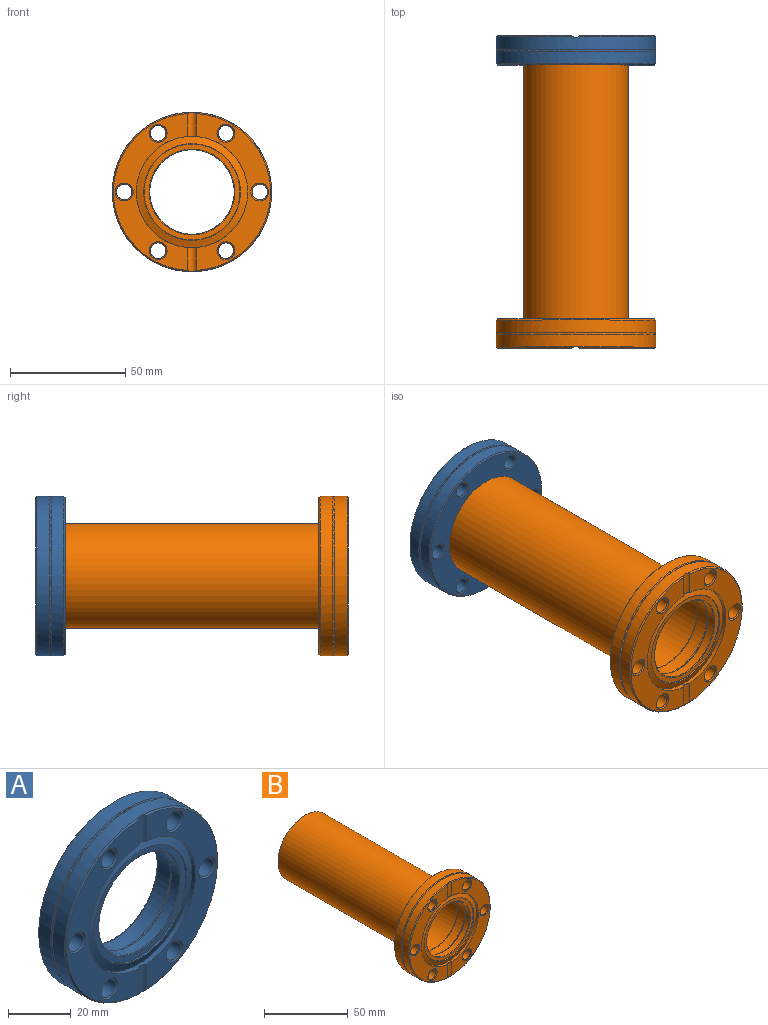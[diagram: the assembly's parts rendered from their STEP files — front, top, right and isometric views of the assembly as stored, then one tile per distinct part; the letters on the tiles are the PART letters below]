
ASSEMBLY  parts=2 mates=1
PART A: 41 faces, bbox 75.3x12.7x75.3 mm
  f0: cylinder r=34.54mm len=69.09mm, axis (0,-1,0), area 1172.5mm2, adj f1,f2,f5,f11,f36
  f1: cylinder r=2.38mm len=10.46mm, axis (0,0,1), area 41.3mm2, adj f0,f2,f3,f4,f5,f6
  f2: cone r=34.54mm half-angle=45deg, axis (0,1,0), area 75.3mm2, adj f0,f1,f3,f11
  f3: plane 67.98x32.27mm, normal (0,-1,0), area 728.6mm2, adj f1,f2,f4,f11,f12,f15,f18
  f4: cylinder r=24.13mm len=48.26mm, axis (0,1,0), area 275.3mm2, adj f1,f3,f6,f11,f38
  f5: cone r=34.54mm half-angle=45deg, axis (0,1,0), area 75.3mm2, adj f0,f1,f6,f11
  f6: plane 67.98x32.27mm, normal (0,-1,0), area 728.6mm2, adj f1,f4,f5,f11,f21,f24,f27
  f7: cylinder r=34.54mm len=69.09mm, axis (0,-1,0), area 1172.5mm2, adj f33,f36
  f8: plane 68.07x68.07mm, normal (0,1,0), area 2139.2mm2, adj f13,f16,f19,f22,f25,f28,f30,f33
  f9: cylinder r=19.18mm len=38.35mm, axis (0,1,0), area 696.9mm2, adj f30,f35
  f10: cylinder r=18.29mm len=36.58mm, axis (0,-1,0), area 423.2mm2, adj f31,f32
  f11: cylinder r=2.38mm len=10.46mm, axis (0,0,-1), area 41.3mm2, adj f0,f2,f3,f4,f5,f6
  f12: cone r=3.87mm half-angle=45deg, axis (0,-1,0), area 16.3mm2, adj f3,f14
  f13: cone r=3.37mm half-angle=45deg, axis (0,1,0), area 16.3mm2, adj f8,f14
  f14: cylinder r=3.37mm len=11.68mm, axis (0,-1,0), area 247.1mm2, adj f12,f13
  f15: cone r=3.87mm half-angle=45deg, axis (0,-1,0), area 16.3mm2, adj f3,f17
  f16: cone r=3.37mm half-angle=45deg, axis (0,1,0), area 16.3mm2, adj f8,f17
  f17: cylinder r=3.37mm len=11.68mm, axis (0,-1,0), area 247.1mm2, adj f15,f16
  f18: cone r=3.87mm half-angle=45deg, axis (0,-1,0), area 16.3mm2, adj f3,f20
  f19: cone r=3.37mm half-angle=45deg, axis (0,1,0), area 16.3mm2, adj f8,f20
  f20: cylinder r=3.37mm len=11.68mm, axis (0,-1,0), area 247.1mm2, adj f18,f19
  f21: cone r=3.87mm half-angle=45deg, axis (0,-1,0), area 16.3mm2, adj f6,f23
  f22: cone r=3.37mm half-angle=45deg, axis (0,1,0), area 16.3mm2, adj f8,f23
  f23: cylinder r=3.37mm len=11.68mm, axis (0,-1,0), area 247.1mm2, adj f21,f22
  f24: cone r=3.87mm half-angle=45deg, axis (0,-1,0), area 16.3mm2, adj f6,f26
  f25: cone r=3.37mm half-angle=45deg, axis (0,1,0), area 16.3mm2, adj f8,f26
  f26: cylinder r=3.37mm len=11.68mm, axis (0,-1,0), area 247.1mm2, adj f24,f25
  f27: cone r=3.87mm half-angle=45deg, axis (0,-1,0), area 16.3mm2, adj f6,f29
  f28: cone r=3.37mm half-angle=45deg, axis (0,1,0), area 16.3mm2, adj f8,f29
  f29: cylinder r=3.37mm len=11.68mm, axis (0,-1,0), area 247.1mm2, adj f27,f28
  f30: torus R=19.69mm, axis (0,1,0), area 97.1mm2, adj f8,f9
  f31: torus R=18.49mm, axis (0,-1,0), area 36.8mm2, adj f10,f40
  f32: torus R=18.54mm, axis (0,1,0), area 46.1mm2, adj f10,f39
  f33: cone r=34.04mm half-angle=45deg, axis (0,-1,0), area 154.8mm2, adj f7,f8
  f34: torus R=19.18mm, axis (0,-1,0), area 99.1mm2, adj f35,f40
  f35: cone r=19.18mm half-angle=32deg, axis (0,-1,0), area 74.1mm2, adj f9,f34
  f36: torus R=34.8mm, axis (0,-1,0), area 229.8mm2, adj f0,f7
  f37: cone r=20.96mm half-angle=20deg, axis (0,-1,0), area 70.9mm2, adj f38,f39
  f38: cone r=24.13mm half-angle=70deg, axis (0,1,0), area 478.6mm2, adj f4,f37
  f39: plane 41.54x41.54mm, normal (0,-1,0), area 275.2mm2, adj f32,f37
  f40: plane 38.35x38.35mm, normal (0,1,0), area 81.2mm2, adj f31,f34
PART B: 44 faces, bbox 75.3x122.7x75.3 mm
  f0: cylinder r=34.54mm len=69.09mm, axis (0,-1,0), area 1172.5mm2, adj f1,f2,f5,f11,f36
  f1: cylinder r=2.38mm len=10.46mm, axis (0,0,1), area 41.3mm2, adj f0,f2,f3,f4,f5,f6
  f2: cone r=34.54mm half-angle=45deg, axis (0,1,0), area 75.3mm2, adj f0,f1,f3,f11
  f3: plane 67.98x32.27mm, normal (0,-1,0), area 728.6mm2, adj f1,f2,f4,f11,f12,f15,f18
  f4: cylinder r=24.13mm len=48.26mm, axis (0,1,0), area 275.3mm2, adj f1,f3,f6,f11,f38
  f5: cone r=34.54mm half-angle=45deg, axis (0,1,0), area 75.3mm2, adj f0,f1,f6,f11
  f6: plane 67.98x32.27mm, normal (0,-1,0), area 728.6mm2, adj f1,f4,f5,f11,f21,f24,f27
  f7: cylinder r=34.54mm len=69.09mm, axis (0,-1,0), area 1172.5mm2, adj f33,f36
  f8: plane 68.07x68.07mm, normal (0,1,0), area 1739.9mm2, adj f13,f16,f19,f22,f25,f28,f33,f42
  f9: cylinder r=19.18mm len=38.35mm, axis (0,1,0), area 696.9mm2, adj f30,f35
  f10: cylinder r=18.29mm len=36.58mm, axis (0,-1,0), area 423.2mm2, adj f31,f32
  f11: cylinder r=2.38mm len=10.46mm, axis (0,0,-1), area 41.3mm2, adj f0,f2,f3,f4,f5,f6
  f12: cone r=3.87mm half-angle=45deg, axis (0,-1,0), area 16.3mm2, adj f3,f14
  f13: cone r=3.37mm half-angle=45deg, axis (0,1,0), area 16.3mm2, adj f8,f14
  f14: cylinder r=3.37mm len=11.68mm, axis (0,-1,0), area 247.1mm2, adj f12,f13
  f15: cone r=3.87mm half-angle=45deg, axis (0,-1,0), area 16.3mm2, adj f3,f17
  f16: cone r=3.37mm half-angle=45deg, axis (0,1,0), area 16.3mm2, adj f8,f17
  f17: cylinder r=3.37mm len=11.68mm, axis (0,-1,0), area 247.1mm2, adj f15,f16
  f18: cone r=3.87mm half-angle=45deg, axis (0,-1,0), area 16.3mm2, adj f3,f20
  f19: cone r=3.37mm half-angle=45deg, axis (0,1,0), area 16.3mm2, adj f8,f20
  f20: cylinder r=3.37mm len=11.68mm, axis (0,-1,0), area 247.1mm2, adj f18,f19
  f21: cone r=3.87mm half-angle=45deg, axis (0,-1,0), area 16.3mm2, adj f6,f23
  f22: cone r=3.37mm half-angle=45deg, axis (0,1,0), area 16.3mm2, adj f8,f23
  f23: cylinder r=3.37mm len=11.68mm, axis (0,-1,0), area 247.1mm2, adj f21,f22
  f24: cone r=3.87mm half-angle=45deg, axis (0,-1,0), area 16.3mm2, adj f6,f26
  f25: cone r=3.37mm half-angle=45deg, axis (0,1,0), area 16.3mm2, adj f8,f26
  f26: cylinder r=3.37mm len=11.68mm, axis (0,-1,0), area 247.1mm2, adj f24,f25
  f27: cone r=3.87mm half-angle=45deg, axis (0,-1,0), area 16.3mm2, adj f6,f29
  f28: cone r=3.37mm half-angle=45deg, axis (0,1,0), area 16.3mm2, adj f8,f29
  f29: cylinder r=3.37mm len=11.68mm, axis (0,-1,0), area 247.1mm2, adj f27,f28
  f30: torus R=19.69mm, axis (0,1,0), area 97.1mm2, adj f9,f41
  f31: torus R=18.49mm, axis (0,-1,0), area 36.8mm2, adj f10,f40
  f32: torus R=18.54mm, axis (0,1,0), area 46.1mm2, adj f10,f39
  f33: cone r=34.04mm half-angle=45deg, axis (0,-1,0), area 154.8mm2, adj f7,f8
  f34: torus R=19.18mm, axis (0,-1,0), area 99.1mm2, adj f35,f40
  f35: cone r=19.18mm half-angle=32deg, axis (0,-1,0), area 74.1mm2, adj f9,f34
  f36: torus R=34.8mm, axis (0,-1,0), area 229.8mm2, adj f0,f7
  f37: cone r=20.96mm half-angle=20deg, axis (0,-1,0), area 70.9mm2, adj f38,f39
  f38: cone r=24.13mm half-angle=70deg, axis (0,1,0), area 478.6mm2, adj f4,f37
  f39: plane 41.54x41.54mm, normal (0,-1,0), area 275.2mm2, adj f32,f37
  f40: plane 38.35x38.35mm, normal (0,1,0), area 81.2mm2, adj f31,f34
  f41: cylinder r=19.69mm len=110mm, axis (0,-1,0), area 13605.3mm2, adj f30,f43
  f42: cylinder r=22.68mm len=110mm, axis (0,-1,0), area 15678.7mm2, adj f8,f43
  f43: plane 45.37x45.37mm, normal (0,1,0), area 399.3mm2, adj f41,f42
PLACE A rot(axis=(1,0,0),180deg) t=(0,122.7,0)mm
PLACE B at identity
MATE fastened A.f9 <-> B.f42  axis (0,-1,0) through (0,116.35,0)mm
